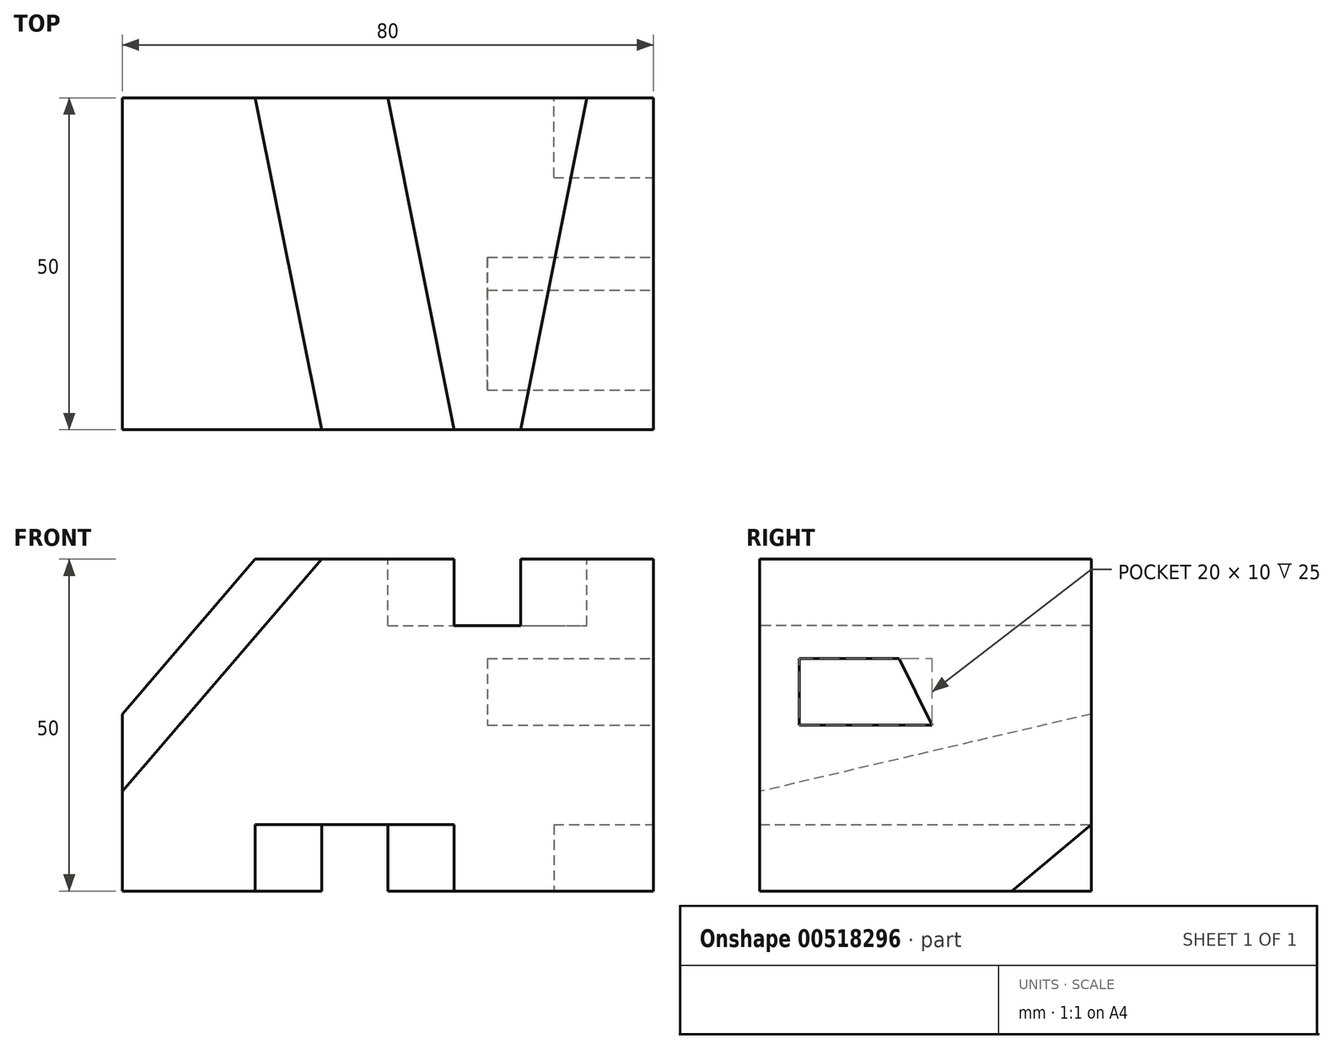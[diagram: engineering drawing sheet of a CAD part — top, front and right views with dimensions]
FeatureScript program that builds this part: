
annotation { "Feature Type Name" : "Feature", "Feature Type Description" : "" }
export const myFeature = defineFeature(function(context is Context, id is Id, definition is map)
    precondition{}
    {
        {
            var Q0;
            Q0=qCreatedBy(makeId("Top.planeOp"),FACE);
            var sketch = newSketch(context, id + "F0", { "sketchPlane" : qUnion([Q0])});
            skLineSegment(sketch, "E0.bottom", {"start": v(0, 0) * mm, "end": v(80, 0) * mm});
            skLineSegment(sketch, "E0.top", {"start": v(0, 50) * mm, "end": v(80, 50) * mm});
            skLineSegment(sketch, "E0.left", {"start": v(0, 0) * mm, "end": v(0, 50) * mm});
            skLineSegment(sketch, "E0.right", {"start": v(80, 0) * mm, "end": v(80, 50) * mm});
            skSolve(sketch);
        }
        {
            var Q0;
            Q0 = qSketchRegion(id + "F0", true);
            extrude(context, id + "F1", {"entities" : qUnion([Q0]), "depth" : 50 * mm, "offsetDistance" : 25 * mm});
        }
        {
            var Q0;
            Q0=makeQuery(id+"F1.opExtrude","SWEPT_FACE",FACE,{"disambiguationData":[OSD([sQuery(id+"F0.wireOp",EDGE,"E0.right")])]});
            var sketch = newSketch(context, id + "F2", { "sketchPlane" : qUnion([Q0])});
            skLineSegment(sketch, "E1", {"start": v(6, 35) * mm, "end": v(6, 25) * mm});
            skLineSegment(sketch, "E2", {"start": v(6, 25) * mm, "end": v(26, 25) * mm});
            skLineSegment(sketch, "E3", {"start": v(26, 25) * mm, "end": v(21, 35) * mm});
            skLineSegment(sketch, "E4", {"start": v(21, 35) * mm, "end": v(6, 35) * mm});
            skSolve(sketch);
        }
        {
            var Q0;
            Q0 = qSketchRegion(id + "F2", true);
            extrude(context, id + "F3", {"entities" : qUnion([Q0]), "operationType" : NewBodyOperationType.REMOVE, "oppositeDirection" : true, "depth" : 25 * mm, "offsetDistance" : 25 * mm});
        }
        {
            var Q0;
            Q0=makeQuery(id+"F1.opExtrude","CAP_FACE",FACE,{"disambiguationData":[OSD([sQuery(id+"F0.wireOp",EDGE,"E0.bottom"),sQuery(id+"F0.wireOp",EDGE,"E0.top"),sQuery(id+"F0.wireOp",EDGE,"E0.left"),sQuery(id+"F0.wireOp",EDGE,"E0.right")])],"isStart":true});
            var sketch = newSketch(context, id + "F4", { "sketchPlane" : qUnion([Q0])});
            skLineSegment(sketch, "E5", {"start": v(20, 0) * mm, "end": v(30, -50) * mm});
            skLineSegment(sketch, "E6", {"start": v(30, -50) * mm, "end": v(40, -50) * mm});
            skLineSegment(sketch, "E7", {"start": v(40, -50) * mm, "end": v(50, 0) * mm});
            skLineSegment(sketch, "E8", {"start": v(50, 0) * mm, "end": v(20, 0) * mm});
            skSolve(sketch);
        }
        {
            var Q0;
            Q0 = qSketchRegion(id + "F4", true);
            extrude(context, id + "F5", {"entities" : qUnion([Q0]), "operationType" : NewBodyOperationType.REMOVE, "oppositeDirection" : true, "depth" : 10 * mm, "offsetDistance" : 25 * mm});
        }
        {
            var Q0;
            Q0=makeQuery(id+"F1.opExtrude","CAP_FACE",FACE,{"disambiguationData":[OSD([sQuery(id+"F0.wireOp",EDGE,"E0.bottom"),sQuery(id+"F0.wireOp",EDGE,"E0.top"),sQuery(id+"F0.wireOp",EDGE,"E0.left"),sQuery(id+"F0.wireOp",EDGE,"E0.right")])],"isStart":false});
            var sketch = newSketch(context, id + "F6", { "sketchPlane" : qUnion([Q0])});
            skLineSegment(sketch, "E9", {"start": v(40, 50) * mm, "end": v(50, 0) * mm});
            skLineSegment(sketch, "E10", {"start": v(50, 0) * mm, "end": v(60, 0) * mm});
            skLineSegment(sketch, "E11", {"start": v(60, 0) * mm, "end": v(70, 50) * mm});
            skLineSegment(sketch, "E12", {"start": v(70, 50) * mm, "end": v(40, 50) * mm});
            skSolve(sketch);
        }
        {
            var Q0;
            Q0 = qSketchRegion(id + "F6", true);
            extrude(context, id + "F7", {"entities" : qUnion([Q0]), "operationType" : NewBodyOperationType.REMOVE, "oppositeDirection" : true, "depth" : 10 * mm, "offsetDistance" : 25 * mm});
        }
        {
            var Q0;
            Q0=makeQuery(id+"F1.opExtrude","SWEPT_FACE",FACE,{"disambiguationData":[OSD([sQuery(id+"F0.wireOp",EDGE,"E0.right")])]});
            var sketch = newSketch(context, id + "F8", { "sketchPlane" : qUnion([Q0])});
            skLineSegment(sketch, "E13", {"start": v(38, 0) * mm, "end": v(50, 10) * mm});
            skSolve(sketch);
        }
        {
            var Q0;
            {var subQ0=sQuery(id+"F8.wireOp",EDGE,"E13");Q0=makeQuery(id+"F8.imprint","IMPRINT",FACE,{"disambiguationData":[TD([[makeQuery(id+"F8.imprint","IMPRINT",EDGE,{"derivedFrom":subQ0}),-1.0]])]});}
            extrude(context, id + "F9", {"entities" : qUnion([Q0]), "operationType" : NewBodyOperationType.REMOVE, "oppositeDirection" : true, "depth" : 15 * mm, "offsetDistance" : 25 * mm});
        }
        {
            var Q0;
            {var subQ0=sQuery(id+"F0.wireOp",EDGE,"E0.bottom");var subQ1=sQuery(id+"F0.wireOp",EDGE,"E0.top");var subQ2=sQuery(id+"F0.wireOp",EDGE,"E0.left");Q0=makeQuery(id+"F7.boolean.opBoolean","SPLIT",FACE,{"disambiguationData":[TD([makeQuery(id+"F1.opExtrude","SWEPT_FACE",FACE,{"disambiguationData":[OSD([subQ2])]})])],"derivedFrom":makeQuery(id+"F1.opExtrude","CAP_FACE",FACE,{"disambiguationData":[OSD([subQ0,subQ1,subQ2,sQuery(id+"F0.wireOp",EDGE,"E0.right")])],"isStart":false})});}
            var sketch = newSketch(context, id + "F10", { "sketchPlane" : qUnion([Q0])});
            skLineSegment(sketch, "E14", {"start": v(30, 0) * mm, "end": v(20, 50) * mm});
            skSolve(sketch);
        }
        {
            var Q0;
            Q0=makeQuery(id+"F1.opExtrude","SWEPT_FACE",FACE,{"disambiguationData":[OSD([sQuery(id+"F0.wireOp",EDGE,"E0.bottom")])]});
            var sketch = newSketch(context, id + "F11", { "sketchPlane" : qUnion([Q0])});
            skLineSegment(sketch, "E15", {"start": v(30, 50) * mm, "end": v(0, 15) * mm});
            skSolve(sketch);
        }
        {
            var Q0;
            {var subQ0=sQuery(id+"F10.wireOp",EDGE,"E14");Q0=makeQuery(id+"F10.imprint","IMPRINT",FACE,{"disambiguationData":[TD([[makeQuery(id+"F10.imprint","IMPRINT",EDGE,{"derivedFrom":subQ0}),1.0]])]});}
            var Q1;
            Q1=sQuery(id+"F11.wireOp",EDGE,"E15");
            sweep(context, id + "F12", {"operationType" : NewBodyOperationType.REMOVE, "profiles" : qUnion([Q0]), "path" : qUnion([Q1])});
        }
    });
